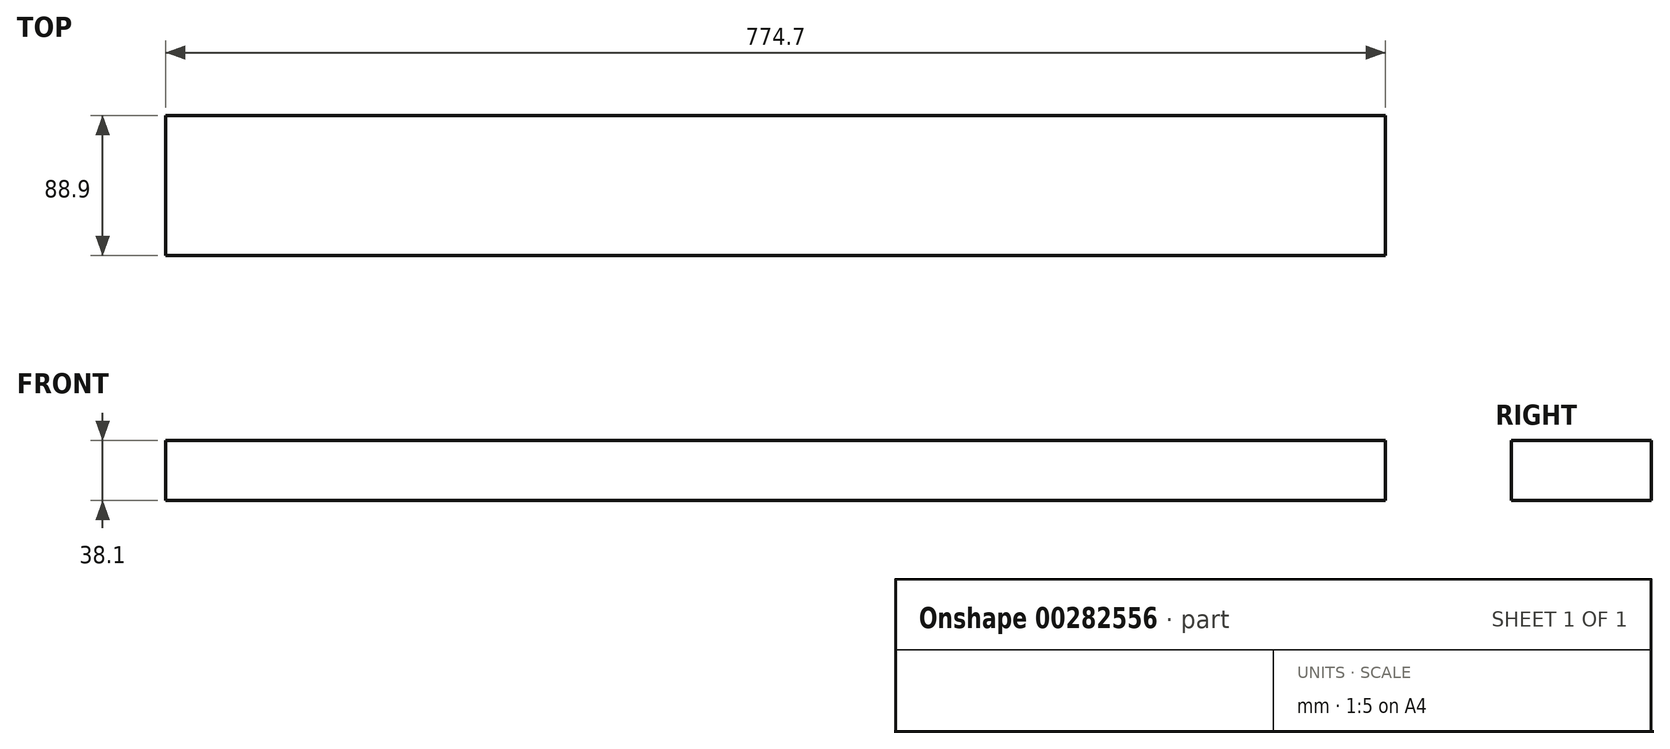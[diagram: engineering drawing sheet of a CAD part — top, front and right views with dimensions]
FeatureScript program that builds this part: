
annotation { "Feature Type Name" : "Feature", "Feature Type Description" : "" }
export const myFeature = defineFeature(function(context is Context, id is Id, definition is map)
    precondition{}
    {
        {
            var Q0;
            Q0=qCreatedBy(makeId("Right.planeOp"),FACE);
            var sketch = newSketch(context, id + "F0", { "sketchPlane" : qUnion([Q0])});
            skLineSegment(sketch, "E0.bottom", {"start": v(0, 0) * mm, "end": v(-88.9, 0) * mm});
            skLineSegment(sketch, "E0.top", {"start": v(0, 38.1) * mm, "end": v(-88.9, 38.1) * mm});
            skLineSegment(sketch, "E0.left", {"start": v(0, 0) * mm, "end": v(0, 38.1) * mm});
            skLineSegment(sketch, "E0.right", {"start": v(-88.9, 0) * mm, "end": v(-88.9, 38.1) * mm});
            skSolve(sketch);
        }
        {
            var Q0;
            Q0 = qSketchRegion(id + "F0", true);
            extrude(context, id + "F1", {"entities" : qUnion([Q0]), "depth" : 774.7 * mm});
        }
    });
